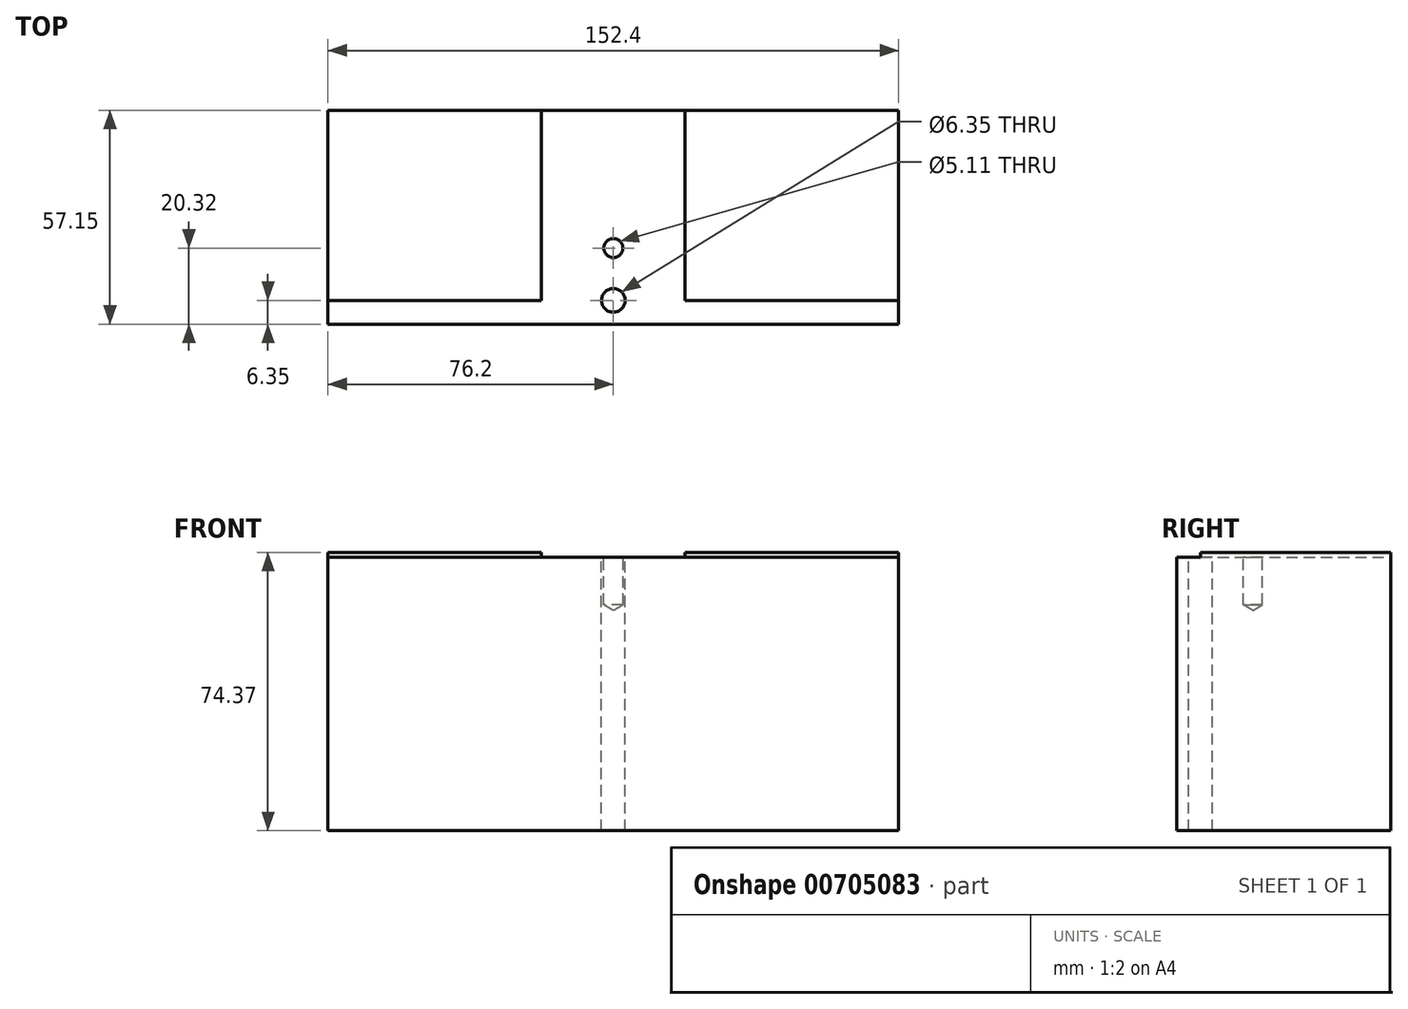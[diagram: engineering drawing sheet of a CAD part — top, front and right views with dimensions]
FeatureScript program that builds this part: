
annotation { "Feature Type Name" : "Feature", "Feature Type Description" : "" }
export const myFeature = defineFeature(function(context is Context, id is Id, definition is map)
    precondition{}
    {
        {
            var Q0;
            Q0=qCreatedBy(makeId("Top.planeOp"),FACE);
            var sketch = newSketch(context, id + "F0", { "sketchPlane" : qUnion([Q0])});
            skLineSegment(sketch, "E0.bottom", {"start": v(0, 0) * mm, "end": v(-152.4, 0) * mm});
            skLineSegment(sketch, "E0.top", {"start": v(0, 57.15) * mm, "end": v(-152.4, 57.15) * mm});
            skLineSegment(sketch, "E0.left", {"start": v(0, 0) * mm, "end": v(0, 57.15) * mm});
            skLineSegment(sketch, "E0.right", {"start": v(-152.4, 0) * mm, "end": v(-152.4, 57.15) * mm});
            skSolve(sketch);
        }
        {
            var Q0;
            Q0=makeQuery(id+"F0.imprint","IMPRINT",FACE,{"disambiguationData":[TD([[makeQuery(id+"F0.imprint","IMPRINT",EDGE,{"derivedFrom":sQuery(id+"F0.wireOp",EDGE,"E0.bottom")}),-1.0]])]});
            extrude(context, id + "F1", {"entities" : qUnion([Q0]), "oppositeDirection" : true, "depth" : 74.37 * mm, "offsetDistance" : 25.4 * mm});
        }
        {
            var Q0;
            Q0=makeQuery(id+"F1.opExtrude","CAP_FACE",FACE,{"disambiguationData":[OSD([sQuery(id+"F0.wireOp",EDGE,"E0.bottom"),sQuery(id+"F0.wireOp",EDGE,"E0.top"),sQuery(id+"F0.wireOp",EDGE,"E0.left"),sQuery(id+"F0.wireOp",EDGE,"E0.right")])],"isStart":true});
            var sketch = newSketch(context, id + "F2", { "sketchPlane" : qUnion([Q0])});
            skLineSegment(sketch, "E1", {"start": v(-152.4, 0) * mm, "end": v(-152.4, 6.35) * mm});
            skLineSegment(sketch, "E2", {"start": v(-152.4, 6.35) * mm, "end": v(0, 6.35) * mm});
            skLineSegment(sketch, "E3", {"start": v(0, 6.35) * mm, "end": v(0, 0) * mm});
            skLineSegment(sketch, "E4", {"start": v(0, 0) * mm, "end": v(-152.4, 0) * mm});
            skSolve(sketch);
        }
        {
            var Q0;
            Q0=makeQuery(id+"F2.imprint","IMPRINT",FACE,{"disambiguationData":[TD([[makeQuery(id+"F2.imprint","IMPRINT",EDGE,{"derivedFrom":sQuery(id+"F2.wireOp",EDGE,"E1")}),-1.0]])]});
            extrude(context, id + "F3", {"entities" : qUnion([Q0]), "operationType" : NewBodyOperationType.REMOVE, "oppositeDirection" : true, "depth" : 1.27 * mm, "offsetDistance" : 25.4 * mm});
        }
        {
            var Q0;
            Q0=makeQuery(id+"F1.opExtrude","CAP_FACE",FACE,{"disambiguationData":[OSD([sQuery(id+"F0.wireOp",EDGE,"E0.bottom"),sQuery(id+"F0.wireOp",EDGE,"E0.top"),sQuery(id+"F0.wireOp",EDGE,"E0.left"),sQuery(id+"F0.wireOp",EDGE,"E0.right")])],"isStart":true});
            var sketch = newSketch(context, id + "F4", { "sketchPlane" : qUnion([Q0])});
            skCircle(sketch, "E5", {"center": v(-76.2, 6.35) * mm, "radius": 3.18 * mm});
            skCircle(sketch, "E6", {"center": v(-76.2, 20.32) * mm, "radius": 2.55 * mm});
            skLineSegment(sketch, "E7", {"start": v(-82.01, 20.32) * mm, "end": v(-69.48, 20.32) * mm});
            skLineSegment(sketch, "E8", {"start": v(-76.2, 26.31) * mm, "end": v(-76.2, 15.53) * mm});
            skSolve(sketch);
        }
        {
            var Q0;
            {var subQ0=sQuery(id+"F4.wireOp",EDGE,"E5");var subQ1=makeQuery(id+"F3.boolean.opBoolean","COPY",EDGE,{"derivedFrom":makeQuery(id+"F3.opExtrude","CAP_EDGE",EDGE,{"disambiguationData":[OSD([sQuery(id+"F2.wireOp",EDGE,"E2")])],"isStart":true})});var subQ2=makeQuery(id+"F4.imprint","INTERSECT",VERTEX,{"disambiguationData":[OD(0.0)],"derivedFrom":[subQ1,subQ0]});Q0=makeQuery(id+"F4.imprint","IMPRINT",FACE,{"disambiguationData":[TD([[makeQuery(id+"F4.imprint","IMPRINT",EDGE,{"disambiguationData":[TD([[subQ2,1.0]])],"derivedFrom":subQ0}),1.0]])]});}
            var Q1;
            {var subQ0=sQuery(id+"F4.wireOp",EDGE,"E5");var subQ1=makeQuery(id+"F3.boolean.opBoolean","COPY",EDGE,{"derivedFrom":makeQuery(id+"F3.opExtrude","CAP_EDGE",EDGE,{"disambiguationData":[OSD([sQuery(id+"F2.wireOp",EDGE,"E2")])],"isStart":true})});var subQ2=makeQuery(id+"F4.imprint","INTERSECT",VERTEX,{"disambiguationData":[OD(0.0)],"derivedFrom":[subQ1,subQ0]});Q1=makeQuery(id+"F4.imprint","IMPRINT",FACE,{"disambiguationData":[TD([[makeQuery(id+"F4.imprint","IMPRINT",EDGE,{"disambiguationData":[TD([[subQ2,-1.0]])],"derivedFrom":subQ0}),1.0]])]});}
            extrude(context, id + "F5", {"entities" : qUnion([Q0, Q1]), "operationType" : NewBodyOperationType.REMOVE, "endBound" : BoundingType.THROUGH_ALL, "oppositeDirection" : true, "depth" : 25.4 * mm, "offsetDistance" : 25.4 * mm});
        }
        {
            var Q0;
            Q0=makeQuery(id+"F1.opExtrude","CAP_FACE",FACE,{"disambiguationData":[OSD([sQuery(id+"F0.wireOp",EDGE,"E0.bottom"),sQuery(id+"F0.wireOp",EDGE,"E0.top"),sQuery(id+"F0.wireOp",EDGE,"E0.left"),sQuery(id+"F0.wireOp",EDGE,"E0.right")])],"isStart":true});
            var sketch = newSketch(context, id + "F6", { "sketchPlane" : qUnion([Q0])});
            skLineSegment(sketch, "E9", {"start": v(-76.2, 6.35) * mm, "end": v(-95.38, 6.35) * mm});
            skLineSegment(sketch, "E10", {"start": v(-76.2, 6.35) * mm, "end": v(-57.02, 6.35) * mm});
            skLineSegment(sketch, "E11", {"start": v(-57.02, 6.35) * mm, "end": v(-57.02, 57.15) * mm});
            skLineSegment(sketch, "E12", {"start": v(-57.02, 57.15) * mm, "end": v(-95.38, 57.15) * mm});
            skLineSegment(sketch, "E13", {"start": v(-95.38, 57.15) * mm, "end": v(-95.38, 6.35) * mm});
            skSolve(sketch);
        }
        {
            var Q0;
            {var subQ0=sQuery(id+"F6.wireOp",EDGE,"E11");Q0=makeQuery(id+"F6.imprint","IMPRINT",FACE,{"disambiguationData":[TD([[makeQuery(id+"F6.imprint","IMPRINT",EDGE,{"derivedFrom":subQ0}),1.0]])]});}
            extrude(context, id + "F7", {"entities" : qUnion([Q0]), "operationType" : NewBodyOperationType.REMOVE, "oppositeDirection" : true, "depth" : 1.27 * mm, "offsetDistance" : 25.4 * mm});
        }
        {
            var Q0;
            Q0=sQuery(id+"F4.wireOp",VERTEX,"E6.center");
            var Q1;
            Q1=makeQuery(id+"F1.opExtrude","SWEPT_BODY",BODY,{"disambiguationData":[OSD([sQuery(id+"F0.wireOp",EDGE,"E0.bottom"),sQuery(id+"F0.wireOp",EDGE,"E0.top"),sQuery(id+"F0.wireOp",EDGE,"E0.left"),sQuery(id+"F0.wireOp",EDGE,"E0.right")])]});
            hole(context, id + "F8", {"style" : HoleStyle.SIMPLE, "endStyle" : HoleEndStyle.BLIND, "holeDiameter" : 5.1 * mm, "majorDiameter" : 6.35 * mm, "holeDepth" : 12.7 * mm, "isTappedThrough" : true, "tappedDepth" : 12.7 * mm, "tapClearance" : 3, "locations" : qUnion([Q0]), "scope" : qUnion([Q1])});
        }
    });
